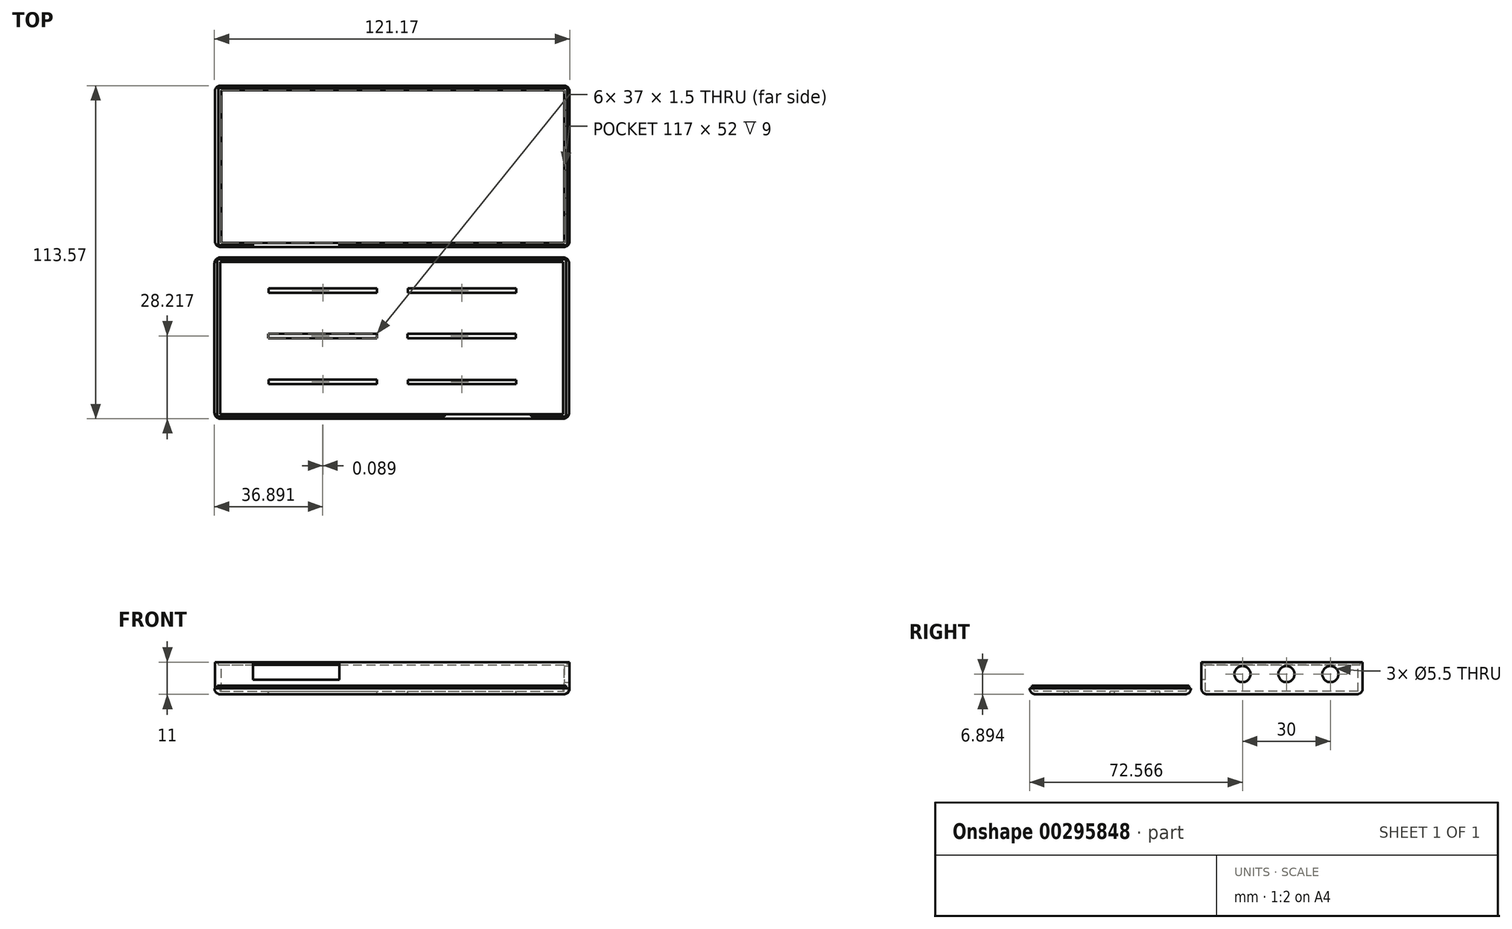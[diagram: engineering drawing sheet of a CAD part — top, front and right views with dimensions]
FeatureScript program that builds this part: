
annotation { "Feature Type Name" : "Feature", "Feature Type Description" : "" }
export const myFeature = defineFeature(function(context is Context, id is Id, definition is map)
    precondition{}
    {
        {
            var Q0;
            Q0=qCreatedBy(makeId("Top.planeOp"),FACE);
            var sketch = newSketch(context, id + "F0", { "sketchPlane" : qUnion([Q0])});
            skLineSegment(sketch, "E0.bottom", {"start": v(-41.81, -29.4) * mm, "end": v(79.19, -29.4) * mm});
            skLineSegment(sketch, "E0.top", {"start": v(-41.81, 25.6) * mm, "end": v(79.19, 25.6) * mm});
            skLineSegment(sketch, "E0.left", {"start": v(-41.81, -29.4) * mm, "end": v(-41.81, 25.6) * mm});
            skLineSegment(sketch, "E0.right", {"start": v(79.19, -29.4) * mm, "end": v(79.19, 25.6) * mm});
            skSolve(sketch);
        }
        {
            var Q0;
            Q0=makeQuery(id+"F0.imprint","IMPRINT",FACE,{"disambiguationData":[TD([[makeQuery(id+"F0.imprint","IMPRINT",EDGE,{"derivedFrom":sQuery(id+"F0.wireOp",EDGE,"E0.bottom")}),1.0]])]});
            extrude(context, id + "F1", {"entities" : qUnion([Q0]), "depth" : 11 * mm, "offsetDistance" : 25 * mm});
        }
        {
            var Q0;
            Q0=makeQuery(id+"F1.opExtrude","SWEPT_FACE",FACE,{"disambiguationData":[OSD([sQuery(id+"F0.wireOp",EDGE,"E0.bottom")])]});
            var sketch = newSketch(context, id + "F2", { "sketchPlane" : qUnion([Q0])});
            skLineSegment(sketch, "E1.bottom", {"start": v(-28.81, 11) * mm, "end": v(0.69, 11) * mm});
            skLineSegment(sketch, "E1.top", {"start": v(-28.81, 5) * mm, "end": v(0.69, 5) * mm});
            skLineSegment(sketch, "E1.left", {"start": v(-28.81, 11) * mm, "end": v(-28.81, 5) * mm});
            skLineSegment(sketch, "E1.right", {"start": v(0.69, 11) * mm, "end": v(0.69, 5) * mm});
            skSolve(sketch);
        }
        {
            var Q0;
            Q0=makeQuery(id+"F2.imprint","IMPRINT",FACE,{"disambiguationData":[TD([[makeQuery(id+"F2.imprint","IMPRINT",EDGE,{"derivedFrom":sQuery(id+"F2.wireOp",EDGE,"E1.bottom")}),-1.0]])]});
            extrude(context, id + "F3", {"entities" : qUnion([Q0]), "operationType" : NewBodyOperationType.REMOVE, "oppositeDirection" : true, "depth" : 51.3 * mm});
        }
        {
            var Q0;
            Q0=makeQuery(id+"F1.opExtrude","CAP_FACE",FACE,{"disambiguationData":[OSD([sQuery(id+"F0.wireOp",EDGE,"E0.bottom"),sQuery(id+"F0.wireOp",EDGE,"E0.top"),sQuery(id+"F0.wireOp",EDGE,"E0.left"),sQuery(id+"F0.wireOp",EDGE,"E0.right")])],"isStart":false});
            var sketch = newSketch(context, id + "F4", { "sketchPlane" : qUnion([Q0])});
            skLineSegment(sketch, "E2.bottom", {"start": v(-39.68, 24.04) * mm, "end": v(77.32, 24.04) * mm});
            skLineSegment(sketch, "E2.top", {"start": v(-39.68, -27.96) * mm, "end": v(77.32, -27.96) * mm});
            skLineSegment(sketch, "E2.left", {"start": v(-39.68, 24.04) * mm, "end": v(-39.68, -27.96) * mm});
            skLineSegment(sketch, "E2.right", {"start": v(77.32, 24.04) * mm, "end": v(77.32, -27.96) * mm});
            skSolve(sketch);
        }
        {
            var Q0;
            Q0=qSketchRegion(id+"F4",true);
            extrude(context, id + "F5", {"entities" : qUnion([Q0]), "operationType" : NewBodyOperationType.REMOVE, "oppositeDirection" : true, "depth" : 10 * mm, "offsetDistance" : 25 * mm});
        }
        {
            var Q0;
            Q0=makeQuery(id+"F1.opExtrude","SWEPT_FACE",FACE,{"disambiguationData":[OSD([sQuery(id+"F0.wireOp",EDGE,"E0.right")])]});
            var sketch = newSketch(context, id + "F6", { "sketchPlane" : qUnion([Q0])});
            skCircle(sketch, "E3", {"center": v(14.6, 6.9) * mm, "radius": 2.75 * mm});
            skCircle(sketch, "E4", {"center": v(-0.4, 6.9) * mm, "radius": 2.75 * mm});
            skCircle(sketch, "E5", {"center": v(-15.4, 6.9) * mm, "radius": 2.75 * mm});
            skSolve(sketch);
        }
        {
            var Q0;
            Q0=qSketchRegion(id+"F6",true);
            extrude(context, id + "F7", {"entities" : qUnion([Q0]), "operationType" : NewBodyOperationType.REMOVE, "oppositeDirection" : true, "depth" : 1.9 * mm});
        }
        {
            var Q0;
            Q0=makeQuery(id+"F1.opExtrude","CAP_FACE",FACE,{"disambiguationData":[OSD([sQuery(id+"F0.wireOp",EDGE,"E0.bottom"),sQuery(id+"F0.wireOp",EDGE,"E0.top"),sQuery(id+"F0.wireOp",EDGE,"E0.left"),sQuery(id+"F0.wireOp",EDGE,"E0.right")])],"isStart":true});
            var Q1;
            Q1=makeQuery(id+"F1.opExtrude","SWEPT_EDGE",EDGE,{"disambiguationData":[OSD([sQuery(id+"F0.wireOp",EDGE,"E0.bottom"),sQuery(id+"F0.wireOp",EDGE,"E0.right")])]});
            var Q2;
            Q2=makeQuery(id+"F1.opExtrude","SWEPT_EDGE",EDGE,{"disambiguationData":[OSD([sQuery(id+"F0.wireOp",EDGE,"E0.top"),sQuery(id+"F0.wireOp",EDGE,"E0.right")])]});
            var Q3;
            Q3=makeQuery(id+"F1.opExtrude","SWEPT_EDGE",EDGE,{"disambiguationData":[OSD([sQuery(id+"F0.wireOp",EDGE,"E0.top"),sQuery(id+"F0.wireOp",EDGE,"E0.left")])]});
            var Q4;
            Q4=makeQuery(id+"F1.opExtrude","SWEPT_EDGE",EDGE,{"disambiguationData":[OSD([sQuery(id+"F0.wireOp",EDGE,"E0.bottom"),sQuery(id+"F0.wireOp",EDGE,"E0.left")])]});
            fillet(context, id + "F8", {"entities" : qUnion([Q0, Q1, Q2, Q3, Q4]), "radius" : 2 * mm, "tangentPropagation" : true, "allowEdgeOverflow" : false});
        }
        {
            var Q0;
            Q0=qCreatedBy(makeId("Top.planeOp"),FACE);
            var sketch = newSketch(context, id + "F9", { "sketchPlane" : qUnion([Q0])});
            skLineSegment(sketch, "E6.bottom", {"start": v(-49.88, -100.26) * mm, "end": v(71.12, -100.26) * mm});
            skLineSegment(sketch, "E6.top", {"start": v(-49.88, -45.26) * mm, "end": v(71.12, -45.26) * mm});
            skLineSegment(sketch, "E6.left", {"start": v(-49.88, -100.26) * mm, "end": v(-49.88, -45.26) * mm});
            skLineSegment(sketch, "E6.right", {"start": v(71.12, -100.26) * mm, "end": v(71.12, -45.26) * mm});
            skSolve(sketch);
        }
        {
            var Q0;
            Q0=makeQuery(id+"F9.imprint","IMPRINT",FACE,{"disambiguationData":[TD([[makeQuery(id+"F9.imprint","IMPRINT",EDGE,{"derivedFrom":sQuery(id+"F9.wireOp",EDGE,"E6.bottom")}),1.0]])]});
            extrude(context, id + "F10", {"entities" : qUnion([Q0]), "depth" : 2 * mm, "offsetDistance" : 25 * mm});
        }
        {
            var Q0;
            Q0=makeQuery(id+"F10.opExtrude","CAP_FACE",FACE,{"disambiguationData":[OSD([sQuery(id+"F9.wireOp",EDGE,"E6.bottom"),sQuery(id+"F9.wireOp",EDGE,"E6.top"),sQuery(id+"F9.wireOp",EDGE,"E6.left"),sQuery(id+"F9.wireOp",EDGE,"E6.right")])],"isStart":false});
            var sketch = newSketch(context, id + "F11", { "sketchPlane" : qUnion([Q0])});
            skLineSegment(sketch, "E7.bottom", {"start": v(-47.88, -46.76) * mm, "end": v(69.12, -46.76) * mm});
            skLineSegment(sketch, "E7.top", {"start": v(-47.88, -98.76) * mm, "end": v(69.12, -98.76) * mm});
            skLineSegment(sketch, "E7.left", {"start": v(-47.88, -46.76) * mm, "end": v(-47.88, -98.76) * mm});
            skLineSegment(sketch, "E7.right", {"start": v(69.12, -46.76) * mm, "end": v(69.12, -98.76) * mm});
            skSolve(sketch);
        }
        {
            var Q0;
            Q0=qSketchRegion(id+"F11",true);
            extrude(context, id + "F12", {"entities" : qUnion([Q0]), "operationType" : NewBodyOperationType.REMOVE, "oppositeDirection" : true, "depth" : 1 * mm, "offsetDistance" : 25 * mm});
        }
        {
            var Q0;
            Q0=makeQuery(id+"F10.opExtrude","CAP_FACE",FACE,{"disambiguationData":[OSD([sQuery(id+"F9.wireOp",EDGE,"E6.bottom"),sQuery(id+"F9.wireOp",EDGE,"E6.top"),sQuery(id+"F9.wireOp",EDGE,"E6.left"),sQuery(id+"F9.wireOp",EDGE,"E6.right")])],"isStart":true});
            var Q1;
            Q1=makeQuery(id+"F10.opExtrude","SWEPT_EDGE",EDGE,{"disambiguationData":[OSD([sQuery(id+"F9.wireOp",EDGE,"E6.bottom"),sQuery(id+"F9.wireOp",EDGE,"E6.left")])]});
            var Q2;
            Q2=makeQuery(id+"F10.opExtrude","SWEPT_EDGE",EDGE,{"disambiguationData":[OSD([sQuery(id+"F9.wireOp",EDGE,"E6.bottom"),sQuery(id+"F9.wireOp",EDGE,"E6.right")])]});
            var Q3;
            Q3=makeQuery(id+"F10.opExtrude","SWEPT_EDGE",EDGE,{"disambiguationData":[OSD([sQuery(id+"F9.wireOp",EDGE,"E6.top"),sQuery(id+"F9.wireOp",EDGE,"E6.right")])]});
            var Q4;
            Q4=makeQuery(id+"F10.opExtrude","SWEPT_EDGE",EDGE,{"disambiguationData":[OSD([sQuery(id+"F9.wireOp",EDGE,"E6.top"),sQuery(id+"F9.wireOp",EDGE,"E6.left")])]});
            fillet(context, id + "F13", {"entities" : qUnion([Q0, Q1, Q2, Q3, Q4]), "radius" : 2 * mm, "tangentPropagation" : true, "allowEdgeOverflow" : false});
        }
        {
            var Q0;
            Q0=makeQuery(id+"F12.boolean.opBoolean","COPY",FACE,{"derivedFrom":makeQuery(id+"F12.opExtrude","CAP_FACE",FACE,{"disambiguationData":[OSD([sQuery(id+"F11.wireOp",EDGE,"E7.bottom"),sQuery(id+"F11.wireOp",EDGE,"E7.top"),sQuery(id+"F11.wireOp",EDGE,"E7.left"),sQuery(id+"F11.wireOp",EDGE,"E7.right")])],"isStart":false})});
            var sketch = newSketch(context, id + "F14", { "sketchPlane" : qUnion([Q0])});
            skLineSegment(sketch, "E8.bottom", {"start": v(-31.4, -55.79) * mm, "end": v(5.6, -55.79) * mm});
            skLineSegment(sketch, "E8.top", {"start": v(-31.4, -57.29) * mm, "end": v(5.6, -57.29) * mm});
            skLineSegment(sketch, "E8.left", {"start": v(-31.4, -55.79) * mm, "end": v(-31.4, -57.29) * mm});
            skLineSegment(sketch, "E8.right", {"start": v(5.6, -55.79) * mm, "end": v(5.6, -57.29) * mm});
            skLineSegment(sketch, "E9.bottom", {"start": v(-31.49, -71.3) * mm, "end": v(5.51, -71.3) * mm});
            skLineSegment(sketch, "E9.top", {"start": v(-31.49, -72.8) * mm, "end": v(5.51, -72.8) * mm});
            skLineSegment(sketch, "E9.left", {"start": v(-31.49, -71.3) * mm, "end": v(-31.49, -72.8) * mm});
            skLineSegment(sketch, "E9.right", {"start": v(5.51, -71.3) * mm, "end": v(5.51, -72.8) * mm});
            skLineSegment(sketch, "E10.bottom", {"start": v(-31.4, -86.95) * mm, "end": v(5.6, -86.95) * mm});
            skLineSegment(sketch, "E10.top", {"start": v(-31.4, -88.45) * mm, "end": v(5.6, -88.45) * mm});
            skLineSegment(sketch, "E10.left", {"start": v(-31.4, -86.95) * mm, "end": v(-31.4, -88.45) * mm});
            skLineSegment(sketch, "E10.right", {"start": v(5.6, -86.95) * mm, "end": v(5.6, -88.45) * mm});
            skLineSegment(sketch, "E11.bottom", {"start": v(16.06, -55.83) * mm, "end": v(53.06, -55.83) * mm});
            skLineSegment(sketch, "E11.top", {"start": v(16.06, -57.33) * mm, "end": v(53.06, -57.33) * mm});
            skLineSegment(sketch, "E11.left", {"start": v(16.06, -55.83) * mm, "end": v(16.06, -57.33) * mm});
            skLineSegment(sketch, "E11.right", {"start": v(53.06, -55.83) * mm, "end": v(53.06, -57.33) * mm});
            skLineSegment(sketch, "E12.bottom", {"start": v(15.97, -71.33) * mm, "end": v(52.97, -71.33) * mm});
            skLineSegment(sketch, "E12.top", {"start": v(15.97, -72.83) * mm, "end": v(52.97, -72.83) * mm});
            skLineSegment(sketch, "E12.left", {"start": v(15.97, -71.33) * mm, "end": v(15.97, -72.83) * mm});
            skLineSegment(sketch, "E12.right", {"start": v(52.97, -71.33) * mm, "end": v(52.97, -72.83) * mm});
            skLineSegment(sketch, "E13.bottom", {"start": v(16.06, -87) * mm, "end": v(53.06, -87) * mm});
            skLineSegment(sketch, "E13.top", {"start": v(16.06, -88.5) * mm, "end": v(53.06, -88.5) * mm});
            skLineSegment(sketch, "E13.left", {"start": v(16.06, -87) * mm, "end": v(16.06, -88.5) * mm});
            skLineSegment(sketch, "E13.right", {"start": v(53.06, -87) * mm, "end": v(53.06, -88.5) * mm});
            skSolve(sketch);
        }
        {
            var Q0;
            Q0=qSketchRegion(id+"F14",true);
            extrude(context, id + "F15", {"entities" : qUnion([Q0]), "operationType" : NewBodyOperationType.REMOVE, "endBound" : BoundingType.THROUGH_ALL, "oppositeDirection" : true, "depth" : 25 * mm});
        }
        {
            var Q0;
            Q0=makeQuery(id+"F10.opExtrude","SWEPT_BODY",BODY,{"disambiguationData":[OSD([sQuery(id+"F9.wireOp",EDGE,"E6.bottom"),sQuery(id+"F9.wireOp",EDGE,"E6.top"),sQuery(id+"F9.wireOp",EDGE,"E6.left"),sQuery(id+"F9.wireOp",EDGE,"E6.right")])]});
            transform(context, id + "F16", {"entities" : qUnion([Q0]), "transformType" : TransformType.TRANSLATION_3D, "dx" : 7.9 * mm, "dy" : 12.3 * mm, "dz" : 0 * mm, "makeCopy" : false});
        }
        {
            var Q0;
            Q0=makeQuery(id+"F10.opExtrude","SWEPT_BODY",BODY,{"disambiguationData":[OSD([sQuery(id+"F9.wireOp",EDGE,"E6.bottom"),sQuery(id+"F9.wireOp",EDGE,"E6.top"),sQuery(id+"F9.wireOp",EDGE,"E6.left"),sQuery(id+"F9.wireOp",EDGE,"E6.right")])]});
            var Q1;
            Q1=makeQuery(id+"F1.opExtrude","SWEPT_BODY",BODY,{"disambiguationData":[OSD([sQuery(id+"F0.wireOp",EDGE,"E0.bottom"),sQuery(id+"F0.wireOp",EDGE,"E0.top"),sQuery(id+"F0.wireOp",EDGE,"E0.left"),sQuery(id+"F0.wireOp",EDGE,"E0.right")])]});
            transform(context, id + "F17", {"entities" : qUnion([Q0, Q1]), "transformType" : TransformType.TRANSLATION_3D, "dx" : 0 * mm, "dy" : 31.1 * mm, "dz" : 0 * mm, "makeCopy" : false});
        }
        {
            var Q0;
            Q0=makeQuery(id+"F0O6dOj11uZ7Y8S_2.boolean.opBoolean","MERGE",FACE,{"derivedFrom":[makeQuery(id+"F5.boolean.opBoolean","COPY",FACE,{"derivedFrom":makeQuery(id+"F5.opExtrude","SWEPT_FACE",FACE,{"disambiguationData":[OSD([sQuery(id+"F4.wireOp",EDGE,"E2.bottom")])]})}),makeQuery(id+"F0O6dOj11uZ7Y8S_2.opExtrude","SWEPT_FACE",FACE,{"disambiguationData":[OSD([sQuery(id+"FnbWpe9698hrVB5_2.wireOp",EDGE,"qNszrat6-i0GZ-uvEl-2yGF-LaZzVx0t4A2u.left")])]})]});
            var sketch = newSketch(context, id + "F18", { "sketchPlane" : qUnion([Q0])});
            skLineSegment(sketch, "E14.bottom", {"start": v(-39.68, 11) * mm, "end": v(77.32, 11) * mm});
            skLineSegment(sketch, "E14.top", {"start": v(-39.68, 10) * mm, "end": v(77.32, 10) * mm});
            skLineSegment(sketch, "E14.left", {"start": v(-39.68, 11) * mm, "end": v(-39.68, 10) * mm});
            skLineSegment(sketch, "E14.right", {"start": v(77.32, 11) * mm, "end": v(77.32, 10) * mm});
            skSolve(sketch);
        }
        {
            var Q0;
            Q0=qSketchRegion(id+"F18",true);
            extrude(context, id + "F19", {"entities" : qUnion([Q0]), "operationType" : NewBodyOperationType.REMOVE, "oppositeDirection" : true, "depth" : .8 * mm, "offsetDistance" : 25 * mm});
        }
        {
            var Q0;
            Q0=makeQuery(id+"F0O6dOj11uZ7Y8S_2.boolean.opBoolean","MERGE",FACE,{"derivedFrom":[makeQuery(id+"F5.boolean.opBoolean","COPY",FACE,{"derivedFrom":makeQuery(id+"F5.opExtrude","SWEPT_FACE",FACE,{"disambiguationData":[OSD([sQuery(id+"F4.wireOp",EDGE,"E2.top")])]})}),makeQuery(id+"F0O6dOj11uZ7Y8S_2.opExtrude","SWEPT_FACE",FACE,{"disambiguationData":[OSD([sQuery(id+"FnbWpe9698hrVB5_2.wireOp",EDGE,"qNszrat6-i0GZ-uvEl-2yGF-LaZzVx0t4A2u.right")])]})]});
            var sketch = newSketch(context, id + "F20", { "sketchPlane" : qUnion([Q0])});
            skLineSegment(sketch, "E15.bottom", {"start": v(39.68, 11) * mm, "end": v(28.81, 11) * mm});
            skLineSegment(sketch, "E15.top", {"start": v(39.68, 10) * mm, "end": v(28.81, 10) * mm});
            skLineSegment(sketch, "E15.left", {"start": v(39.68, 11) * mm, "end": v(39.68, 10) * mm});
            skLineSegment(sketch, "E15.right", {"start": v(28.81, 11) * mm, "end": v(28.81, 10) * mm});
            skLineSegment(sketch, "E16.bottom", {"start": v(-0.69, 11) * mm, "end": v(-78.33, 11) * mm});
            skLineSegment(sketch, "E16.top", {"start": v(-0.69, 10) * mm, "end": v(-78.33, 10) * mm});
            skLineSegment(sketch, "E16.left", {"start": v(-0.69, 11) * mm, "end": v(-0.69, 10) * mm});
            skLineSegment(sketch, "E16.right", {"start": v(-78.33, 11) * mm, "end": v(-78.33, 10) * mm});
            skSolve(sketch);
        }
        {
            var Q0;
            Q0=qSketchRegion(id+"F20",true);
            extrude(context, id + "F21", {"entities" : qUnion([Q0]), "operationType" : NewBodyOperationType.REMOVE, "oppositeDirection" : true, "depth" : .8 * mm});
        }
        {
            var Q0;
            Q0=makeQuery(id+"F21.boolean.opBoolean","MERGE",FACE,{"derivedFrom":[makeQuery(id+"F19.boolean.opBoolean","MERGE",FACE,{"derivedFrom":[makeQuery(id+"F5.boolean.opBoolean","COPY",FACE,{"derivedFrom":makeQuery(id+"F5.opExtrude","SWEPT_FACE",FACE,{"disambiguationData":[OSD([sQuery(id+"F4.wireOp",EDGE,"E2.left")])]})}),makeQuery(id+"F19.opExtrude","SWEPT_FACE",FACE,{"disambiguationData":[OSD([sQuery(id+"F18.wireOp",EDGE,"E14.left")])]})]}),makeQuery(id+"F21.opExtrude","SWEPT_FACE",FACE,{"disambiguationData":[OSD([sQuery(id+"F20.wireOp",EDGE,"E15.left")])]})]});
            var sketch = newSketch(context, id + "F22", { "sketchPlane" : qUnion([Q0])});
            skLineSegment(sketch, "E17.bottom", {"start": v(2.34, 11) * mm, "end": v(55.94, 11) * mm});
            skLineSegment(sketch, "E17.top", {"start": v(2.34, 10) * mm, "end": v(55.94, 10) * mm});
            skLineSegment(sketch, "E17.left", {"start": v(2.34, 11) * mm, "end": v(2.34, 10) * mm});
            skLineSegment(sketch, "E17.right", {"start": v(55.94, 11) * mm, "end": v(55.94, 10) * mm});
            skSolve(sketch);
        }
        {
            var Q0;
            Q0=qSketchRegion(id+"F22",true);
            extrude(context, id + "F23", {"entities" : qUnion([Q0]), "operationType" : NewBodyOperationType.REMOVE, "oppositeDirection" : true, "depth" : 1 * mm});
        }
        {
            var Q0;
            Q0=makeQuery(id+"F10.opExtrude","CAP_FACE",FACE,{"disambiguationData":[OSD([sQuery(id+"F9.wireOp",EDGE,"E6.bottom"),sQuery(id+"F9.wireOp",EDGE,"E6.top"),sQuery(id+"F9.wireOp",EDGE,"E6.left"),sQuery(id+"F9.wireOp",EDGE,"E6.right")])],"isStart":false});
            var sketch = newSketch(context, id + "F24", { "sketchPlane" : qUnion([Q0])});
            skLineSegment(sketch, "E18.bottom", {"start": v(77.02, -3.36) * mm, "end": v(78.02, -3.36) * mm});
            skLineSegment(sketch, "E18.top", {"start": v(77.02, -55.36) * mm, "end": v(78.02, -55.36) * mm});
            skLineSegment(sketch, "E18.left", {"start": v(77.02, -3.36) * mm, "end": v(77.02, -55.36) * mm});
            skLineSegment(sketch, "E18.right", {"start": v(78.02, -3.36) * mm, "end": v(78.02, -55.36) * mm});
            skLineSegment(sketch, "E19.bottom", {"start": v(-39.98, -3.36) * mm, "end": v(-40.98, -3.36) * mm});
            skLineSegment(sketch, "E19.top", {"start": v(-39.98, -55.36) * mm, "end": v(-40.98, -55.36) * mm});
            skLineSegment(sketch, "E19.left", {"start": v(-39.98, -3.36) * mm, "end": v(-39.98, -55.36) * mm});
            skLineSegment(sketch, "E19.right", {"start": v(-40.98, -3.36) * mm, "end": v(-40.98, -55.36) * mm});
            skLineSegment(sketch, "E20.bottom", {"start": v(-40.98, -3.36) * mm, "end": v(78.02, -3.36) * mm});
            skLineSegment(sketch, "E20.top", {"start": v(-40.98, -2.56) * mm, "end": v(78.02, -2.56) * mm});
            skLineSegment(sketch, "E20.left", {"start": v(-40.98, -3.36) * mm, "end": v(-40.98, -2.56) * mm});
            skLineSegment(sketch, "E20.right", {"start": v(78.02, -3.36) * mm, "end": v(78.02, -2.56) * mm});
            skLineSegment(sketch, "E21.bottom", {"start": v(-40.98, -55.36) * mm, "end": v(78.02, -55.36) * mm});
            skLineSegment(sketch, "E21.top", {"start": v(-40.98, -56.16) * mm, "end": v(78.02, -56.16) * mm});
            skLineSegment(sketch, "E21.left", {"start": v(-40.98, -55.36) * mm, "end": v(-40.98, -56.16) * mm});
            skLineSegment(sketch, "E21.right", {"start": v(78.02, -55.36) * mm, "end": v(78.02, -56.16) * mm});
            skSolve(sketch);
        }
        {
            var Q0;
            Q0=qSketchRegion(id+"F24",true);
            extrude(context, id + "F25", {"entities" : qUnion([Q0]), "operationType" : NewBodyOperationType.ADD, "depth" : 1 * mm, "offsetDistance" : 25 * mm});
        }
        {
            var Q0;
            Q0=makeQuery(id+"F25.opExtrude","SWEPT_FACE",FACE,{"disambiguationData":[OSD([sQuery(id+"F24.wireOp",EDGE,"E21.top")])]});
            var sketch = newSketch(context, id + "F26", { "sketchPlane" : qUnion([Q0])});
            skLineSegment(sketch, "E22.bottom", {"start": v(66.02, 2) * mm, "end": v(36.52, 2) * mm});
            skLineSegment(sketch, "E22.top", {"start": v(66.02, 3) * mm, "end": v(36.52, 3) * mm});
            skLineSegment(sketch, "E22.left", {"start": v(66.02, 2) * mm, "end": v(66.02, 3) * mm});
            skLineSegment(sketch, "E22.right", {"start": v(36.52, 2) * mm, "end": v(36.52, 3) * mm});
            skSolve(sketch);
        }
        {
            var Q0;
            Q0=qSketchRegion(id+"F26",true);
            extrude(context, id + "F27", {"entities" : qUnion([Q0]), "operationType" : NewBodyOperationType.REMOVE, "oppositeDirection" : true, "depth" : 1 * mm});
        }
        {
            var Q0;
            Q0=makeQuery(id+"F19.boolean.opBoolean","MERGE",FACE,{"derivedFrom":[makeQuery(id+"F5.boolean.opBoolean","COPY",FACE,{"derivedFrom":makeQuery(id+"F5.opExtrude","SWEPT_FACE",FACE,{"disambiguationData":[OSD([sQuery(id+"F4.wireOp",EDGE,"E2.right")])]})}),makeQuery(id+"F19.opExtrude","SWEPT_FACE",FACE,{"disambiguationData":[OSD([sQuery(id+"F18.wireOp",EDGE,"E14.right")])]})]});
            var sketch = newSketch(context, id + "F28", { "sketchPlane" : qUnion([Q0])});
            skLineSegment(sketch, "E23.bottom", {"start": v(-55.94, 11) * mm, "end": v(-3.78, 11) * mm});
            skLineSegment(sketch, "E23.top", {"start": v(-55.94, 10) * mm, "end": v(-3.78, 10) * mm});
            skLineSegment(sketch, "E23.left", {"start": v(-55.94, 11) * mm, "end": v(-55.94, 10) * mm});
            skLineSegment(sketch, "E23.right", {"start": v(-3.78, 11) * mm, "end": v(-3.78, 10) * mm});
            skSolve(sketch);
        }
        {
            var Q0;
            Q0 = qSketchRegion(id + "F28", true);
            extrude(context, id + "F29", {"entities" : qUnion([Q0]), "operationType" : NewBodyOperationType.REMOVE, "oppositeDirection" : true, "depth" : 1 * mm, "offsetDistance" : 25 * mm});
        }
        {
            var Q0;
            Q0=makeQuery(id+"F1.opExtrude","CAP_FACE",FACE,{"disambiguationData":[OSD([sQuery(id+"F0.wireOp",EDGE,"E0.bottom"),sQuery(id+"F0.wireOp",EDGE,"E0.top"),sQuery(id+"F0.wireOp",EDGE,"E0.left"),sQuery(id+"F0.wireOp",EDGE,"E0.right")])],"isStart":false});
            var sketch = newSketch(context, id + "F30", { "sketchPlane" : qUnion([Q0])});
            skLineSegment(sketch, "E24.bottom", {"start": v(78.32, 3.78) * mm, "end": v(77.32, 3.78) * mm});
            skLineSegment(sketch, "E24.top", {"start": v(78.32, 3.03) * mm, "end": v(77.32, 3.03) * mm});
            skLineSegment(sketch, "E24.left", {"start": v(78.32, 3.78) * mm, "end": v(78.32, 3.03) * mm});
            skLineSegment(sketch, "E24.right", {"start": v(77.32, 3.78) * mm, "end": v(77.32, 3.03) * mm});
            skSolve(sketch);
        }
        {
            var Q0;
            Q0 = qSketchRegion(id + "F30", true);
            extrude(context, id + "F31", {"entities" : qUnion([Q0]), "operationType" : NewBodyOperationType.REMOVE, "oppositeDirection" : true, "depth" : 1 * mm, "offsetDistance" : 25 * mm});
        }
    });
